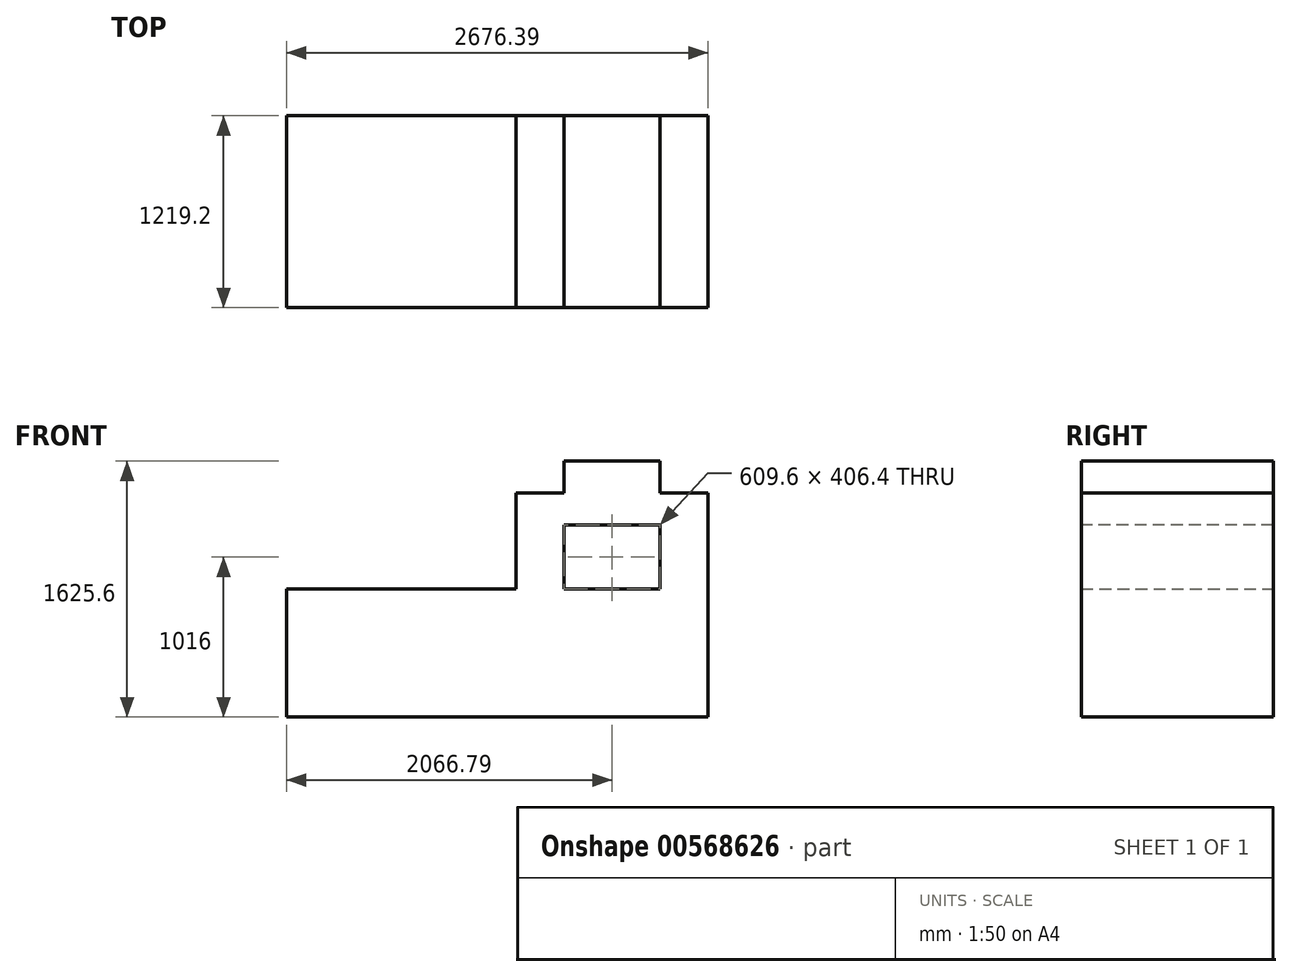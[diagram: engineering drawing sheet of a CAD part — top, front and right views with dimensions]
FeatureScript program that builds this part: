
annotation { "Feature Type Name" : "Feature", "Feature Type Description" : "" }
export const myFeature = defineFeature(function(context is Context, id is Id, definition is map)
    precondition{}
    {
        {
            var Q0;
            Q0=qCreatedBy(makeId("Front.planeOp"),FACE);
            var sketch = newSketch(context, id + "F0", { "sketchPlane" : qUnion([Q0])});
            skLineSegment(sketch, "E0", {"start": v(-66.8, 17.5) * mm, "end": v(2676.4, 17.5) * mm});
            skLineSegment(sketch, "E1", {"start": v(2676.4, 17.5) * mm, "end": v(2676.4, 1643.1) * mm});
            skLineSegment(sketch, "E2", {"start": v(2676.4, 1643.1) * mm, "end": v(1457.2, 1643.1) * mm});
            skLineSegment(sketch, "E3", {"start": v(1457.2, 1643.1) * mm, "end": v(1457.2, 830.3) * mm});
            skLineSegment(sketch, "E4", {"start": v(1457.2, 830.3) * mm, "end": v(0, 830.3) * mm});
            skLineSegment(sketch, "E5", {"start": v(0, 830.3) * mm, "end": v(0, 0) * mm});
            skSolve(sketch);
        }
        {
            var Q0;
            Q0 = qSketchRegion(id + "F0", true);
            extrude(context, id + "F1", {"entities" : qUnion([Q0]), "depth" : 1219.2 * mm, "offsetDistance" : 25.4 * mm});
        }
        {
            var Q0;
            Q0=makeQuery(id+"F1.opExtrude","CAP_FACE",FACE,{"disambiguationData":[OSD([sQuery(id+"F0.wireOp",EDGE,"E0"),sQuery(id+"F0.wireOp",EDGE,"E1"),sQuery(id+"F0.wireOp",EDGE,"E2"),sQuery(id+"F0.wireOp",EDGE,"E3"),sQuery(id+"F0.wireOp",EDGE,"E4"),sQuery(id+"F0.wireOp",EDGE,"E5")])],"isStart":false});
            var sketch = newSketch(context, id + "F2", { "sketchPlane" : qUnion([Q0])});
            skLineSegment(sketch, "E6.bottom", {"start": v(1457.2, 1643.1) * mm, "end": v(1762, 1643.1) * mm});
            skLineSegment(sketch, "E6.top", {"start": v(1457.2, 1439.9) * mm, "end": v(1762, 1439.9) * mm});
            skLineSegment(sketch, "E6.left", {"start": v(1457.2, 1643.1) * mm, "end": v(1457.2, 1439.9) * mm});
            skLineSegment(sketch, "E6.right", {"start": v(1762, 1643.1) * mm, "end": v(1762, 1439.9) * mm});
            skSolve(sketch);
        }
        {
            var Q0;
            Q0=makeQuery(id+"F2.imprint","IMPRINT",FACE,{"disambiguationData":[TD([[makeQuery(id+"F2.imprint","IMPRINT",EDGE,{"derivedFrom":sQuery(id+"F2.wireOp",EDGE,"E6.bottom")}),1.0]])]});
            extrude(context, id + "F3", {"entities" : qUnion([Q0]), "operationType" : NewBodyOperationType.REMOVE, "endBound" : BoundingType.UP_TO_NEXT, "oppositeDirection" : true, "depth" : 25.4 * mm, "offsetDistance" : 25.4 * mm});
        }
        {
            var Q0;
            Q0=makeQuery(id+"F1.opExtrude","CAP_FACE",FACE,{"disambiguationData":[OSD([sQuery(id+"F0.wireOp",EDGE,"E0"),sQuery(id+"F0.wireOp",EDGE,"E1"),sQuery(id+"F0.wireOp",EDGE,"E2"),sQuery(id+"F0.wireOp",EDGE,"E3"),sQuery(id+"F0.wireOp",EDGE,"E4"),sQuery(id+"F0.wireOp",EDGE,"E5")])],"isStart":false});
            var sketch = newSketch(context, id + "F4", { "sketchPlane" : qUnion([Q0])});
            skLineSegment(sketch, "E7.bottom", {"start": v(2676.4, 1643.1) * mm, "end": v(2371.6, 1643.1) * mm});
            skLineSegment(sketch, "E7.top", {"start": v(2676.4, 1439.9) * mm, "end": v(2371.6, 1439.9) * mm});
            skLineSegment(sketch, "E7.left", {"start": v(2676.4, 1643.1) * mm, "end": v(2676.4, 1439.9) * mm});
            skLineSegment(sketch, "E7.right", {"start": v(2371.6, 1643.1) * mm, "end": v(2371.6, 1439.9) * mm});
            skSolve(sketch);
        }
        {
            var Q0;
            Q0 = qSketchRegion(id + "F4", true);
            extrude(context, id + "F5", {"entities" : qUnion([Q0]), "operationType" : NewBodyOperationType.REMOVE, "endBound" : BoundingType.THROUGH_ALL, "oppositeDirection" : true, "depth" : 25.4 * mm, "offsetDistance" : 25.4 * mm});
        }
        {
            var Q0;
            Q0=makeQuery(id+"F1.opExtrude","SWEPT_FACE",FACE,{"disambiguationData":[OSD([sQuery(id+"F0.wireOp",EDGE,"E4")])]});
            var sketch = newSketch(context, id + "F6", { "sketchPlane" : qUnion([Q0])});
            skSolve(sketch);
        }
        {
            var Q0;
            Q0=makeQuery(id+"F1.opExtrude","CAP_FACE",FACE,{"disambiguationData":[OSD([sQuery(id+"F0.wireOp",EDGE,"E0"),sQuery(id+"F0.wireOp",EDGE,"E1"),sQuery(id+"F0.wireOp",EDGE,"E2"),sQuery(id+"F0.wireOp",EDGE,"E3"),sQuery(id+"F0.wireOp",EDGE,"E4"),sQuery(id+"F0.wireOp",EDGE,"E5")])],"isStart":false});
            var sketch = newSketch(context, id + "F7", { "sketchPlane" : qUnion([Q0])});
            skLineSegment(sketch, "E8.bottom", {"start": v(2371.6, 1236.7) * mm, "end": v(1762, 1236.7) * mm});
            skLineSegment(sketch, "E8.top", {"start": v(2371.6, 830.3) * mm, "end": v(1762, 830.3) * mm});
            skLineSegment(sketch, "E8.left", {"start": v(2371.6, 1236.7) * mm, "end": v(2371.6, 830.3) * mm});
            skLineSegment(sketch, "E8.right", {"start": v(1762, 1236.7) * mm, "end": v(1762, 830.3) * mm});
            skSolve(sketch);
        }
        {
            var Q0;
            Q0 = qSketchRegion(id + "F7", true);
            extrude(context, id + "F8", {"entities" : qUnion([Q0]), "operationType" : NewBodyOperationType.REMOVE, "endBound" : BoundingType.THROUGH_ALL, "oppositeDirection" : true, "depth" : 25.4 * mm, "offsetDistance" : 25.4 * mm});
        }
    });
